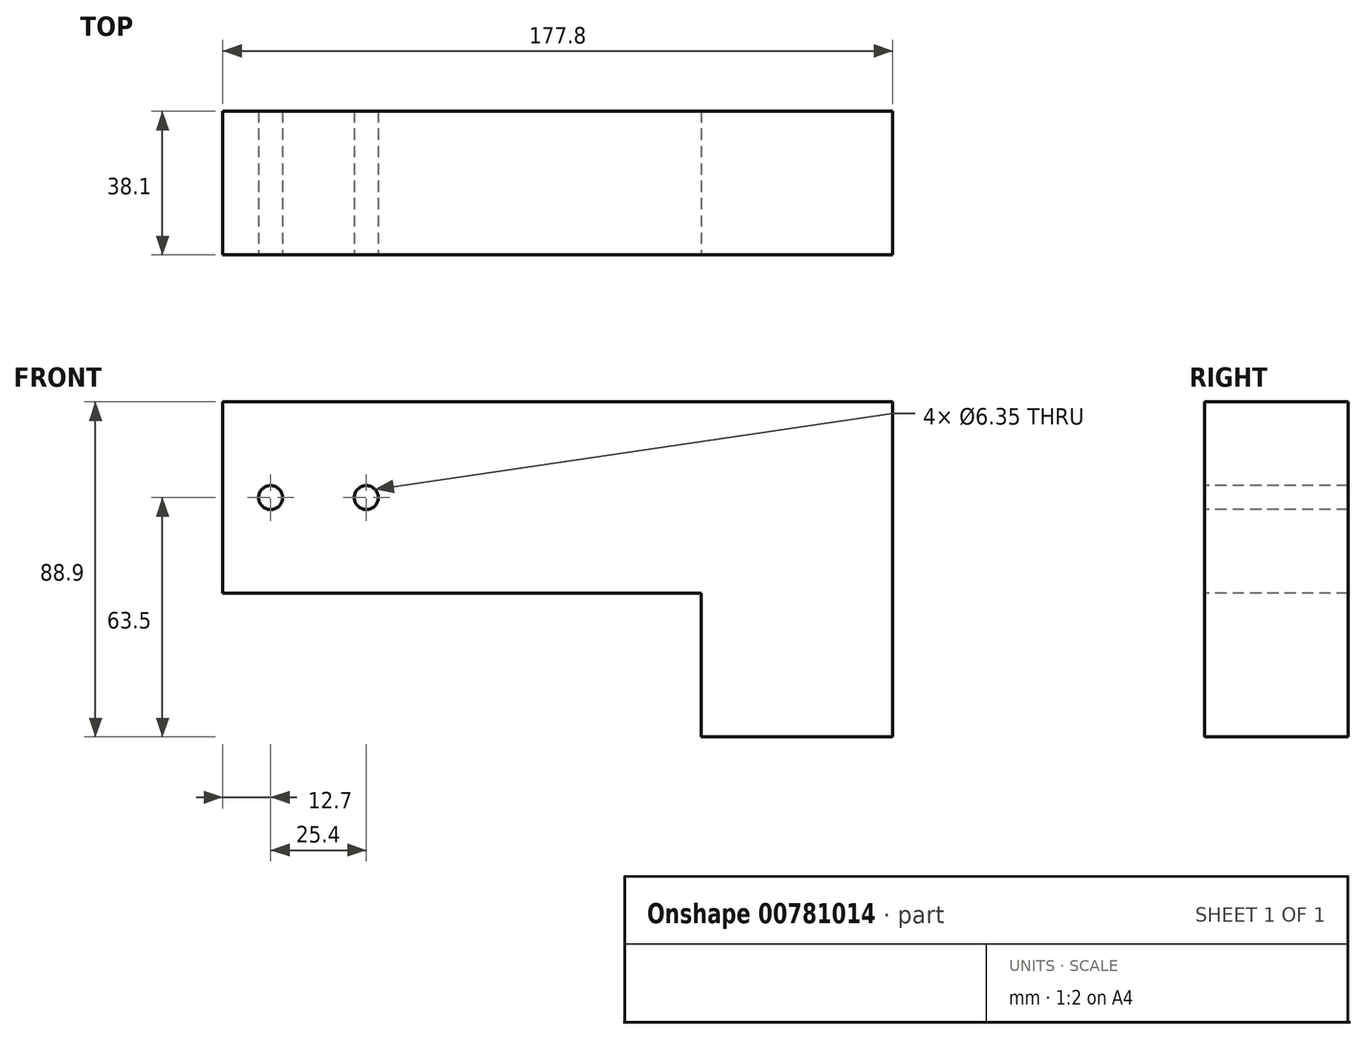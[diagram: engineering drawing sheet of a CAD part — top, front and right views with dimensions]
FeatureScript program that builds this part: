
annotation { "Feature Type Name" : "Feature", "Feature Type Description" : "" }
export const myFeature = defineFeature(function(context is Context, id is Id, definition is map)
    precondition{}
    {
        {
            var Q0;
            Q0=qCreatedBy(makeId("Top.planeOp"),FACE);
            var sketch = newSketch(context, id + "F0", { "sketchPlane" : qUnion([Q0])});
            skLineSegment(sketch, "E0", {"start": v(0, 0) * mm, "end": v(0, -38.1) * mm});
            skLineSegment(sketch, "E1", {"start": v(177.8, -38.1) * mm, "end": v(0, -38.1) * mm});
            skLineSegment(sketch, "E2", {"start": v(177.8, 0) * mm, "end": v(0, 0) * mm});
            skLineSegment(sketch, "E3", {"start": v(177.8, -38.1) * mm, "end": v(177.8, 0) * mm});
            skSolve(sketch);
        }
        {
            var Q0;
            Q0=makeQuery(id+"F0.imprint","IMPRINT",FACE,{"disambiguationData":[TD([[makeQuery(id+"F0.imprint","IMPRINT",EDGE,{"derivedFrom":sQuery(id+"F0.wireOp",EDGE,"E0")}),1.0]])]});
            extrude(context, id + "F1", {"entities" : qUnion([Q0]), "depth" : 88.9 * mm, "offsetDistance" : 25.4 * mm});
        }
        {
            var Q0;
            Q0=makeQuery(id+"F1.opExtrude","SWEPT_FACE",FACE,{"disambiguationData":[OSD([sQuery(id+"F0.wireOp",EDGE,"E1")])]});
            var sketch = newSketch(context, id + "F2", { "sketchPlane" : qUnion([Q0])});
            skLineSegment(sketch, "E4", {"start": v(127, 0) * mm, "end": v(127, 38.1) * mm});
            skLineSegment(sketch, "E5", {"start": v(127, 38.1) * mm, "end": v(0, 38.1) * mm});
            skSolve(sketch);
        }
        {
            var Q0;
            {var subQ0=sQuery(id+"F2.wireOp",EDGE,"E4");Q0=makeQuery(id+"F2.imprint","IMPRINT",FACE,{"disambiguationData":[TD([[makeQuery(id+"F2.imprint","IMPRINT",EDGE,{"derivedFrom":subQ0}),1.0]])]});}
            extrude(context, id + "F3", {"entities" : qUnion([Q0]), "operationType" : NewBodyOperationType.REMOVE, "endBound" : BoundingType.THROUGH_ALL, "oppositeDirection" : true, "depth" : 25.4 * mm, "offsetDistance" : 25.4 * mm});
        }
        {
            var Q0;
            Q0=makeQuery(id+"F1.opExtrude","SWEPT_FACE",FACE,{"disambiguationData":[OSD([sQuery(id+"F0.wireOp",EDGE,"E1")])]});
            var sketch = newSketch(context, id + "F4", { "sketchPlane" : qUnion([Q0])});
            skLineSegment(sketch, "E6", {"start": v(0, 63.5) * mm, "end": v(133.08, 63.5) * mm, "construction": true});
            skPoint(sketch, "E7", {"position": v(12.7, 63.5) * mm});
            skPoint(sketch, "E8", {"position": v(38.1, 63.5) * mm});
            skSolve(sketch);
        }
        {
            var Q0;
            Q0=sQuery(id+"F4.wireOp",VERTEX,"E8");
            var Q1;
            Q1=sQuery(id+"F4.wireOp",VERTEX,"E7");
            var Q2;
            Q2=makeQuery(id+"F1.opExtrude","SWEPT_BODY",BODY,{"disambiguationData":[OSD([sQuery(id+"F0.wireOp",EDGE,"E0"),sQuery(id+"F0.wireOp",EDGE,"E1"),sQuery(id+"F0.wireOp",EDGE,"E2"),sQuery(id+"F0.wireOp",EDGE,"E3")])]});
            hole(context, id + "F5", {"style" : HoleStyle.SIMPLE, "endStyle" : HoleEndStyle.THROUGH, "holeDiameter" : 6.35 * mm, "majorDiameter" : 6.35 * mm, "isTappedThrough" : true, "tappedDepth" : 12.7 * mm, "tapClearance" : 3, "locations" : qUnion([Q0, Q1]), "scope" : qUnion([Q2])});
        }
    });
